# Revit family: Electrical-Box_FSR_T3CRST
name_source: partatom
category: Electrical Fixtures
units: mm (PartAtom-declared; Revit-internal decimal feet)

## family parameters
Always vertical = No
Classification Number = 23.85.10.17.11
Cut with Voids When Loaded = No
Maintain Annotation Orientation = No
Part Type = Normal
Room Calculation Point = No
Round Connector Dimension = Use Diameter
Shared = No
Work Plane-Based = Yes

## types (3) — shared parameters
Assembly Code = D5020100
Body Material = Jack - As Specified
Construction Details = ftp://doclib.fsrinc.com/
Default Elevation = 48"
Device 1 = Device : Crestron TPS Block-10TM RJ45
Device 2 = Device : None
Device 3 = Device : None
Device 4 = Device : None
Device 5 = Device : None
Device 6 = Device : None
Green Building-LEED = http://www.arcat.com
Installation_Fabricaton = ftp://doclib.fsrinc.com/
Keynote = 26 27 26
Manufacturer = FSR Inc.
Manufacturer Fax = 973-785-4207
Manufacturer Website = http://www.fsrinc.com
Model = T3-CRST
Product Data = http://www.arcat.com
Sales Information = http://www.fsrinc.com
Send Message = http://admin.arcat.com
Specification = http://www.arcat.com
Test Data = ftp://doclib.fsrinc.com/
URL = http://www.fsrinc.com
zero-valued in all types: Expected Lifespan (Years), Maintenance Schedule (Months), Warranty Duration (Years)

## per-type parameters (varying)
| type | Cover Material | Description |
| Brass Cover | Brass | FSR T3-CRST - Brass Cover |
| Aluminum Cover | Aluminum | FSR T3-CRST - Aluminum Cover |
| Black Cover | Black | FSR T3-CRST - Black Cover |

## geometry (parser evidence)
native form markers: Blend x10, Sweep x5
no freeform markers — native parametric forms only
